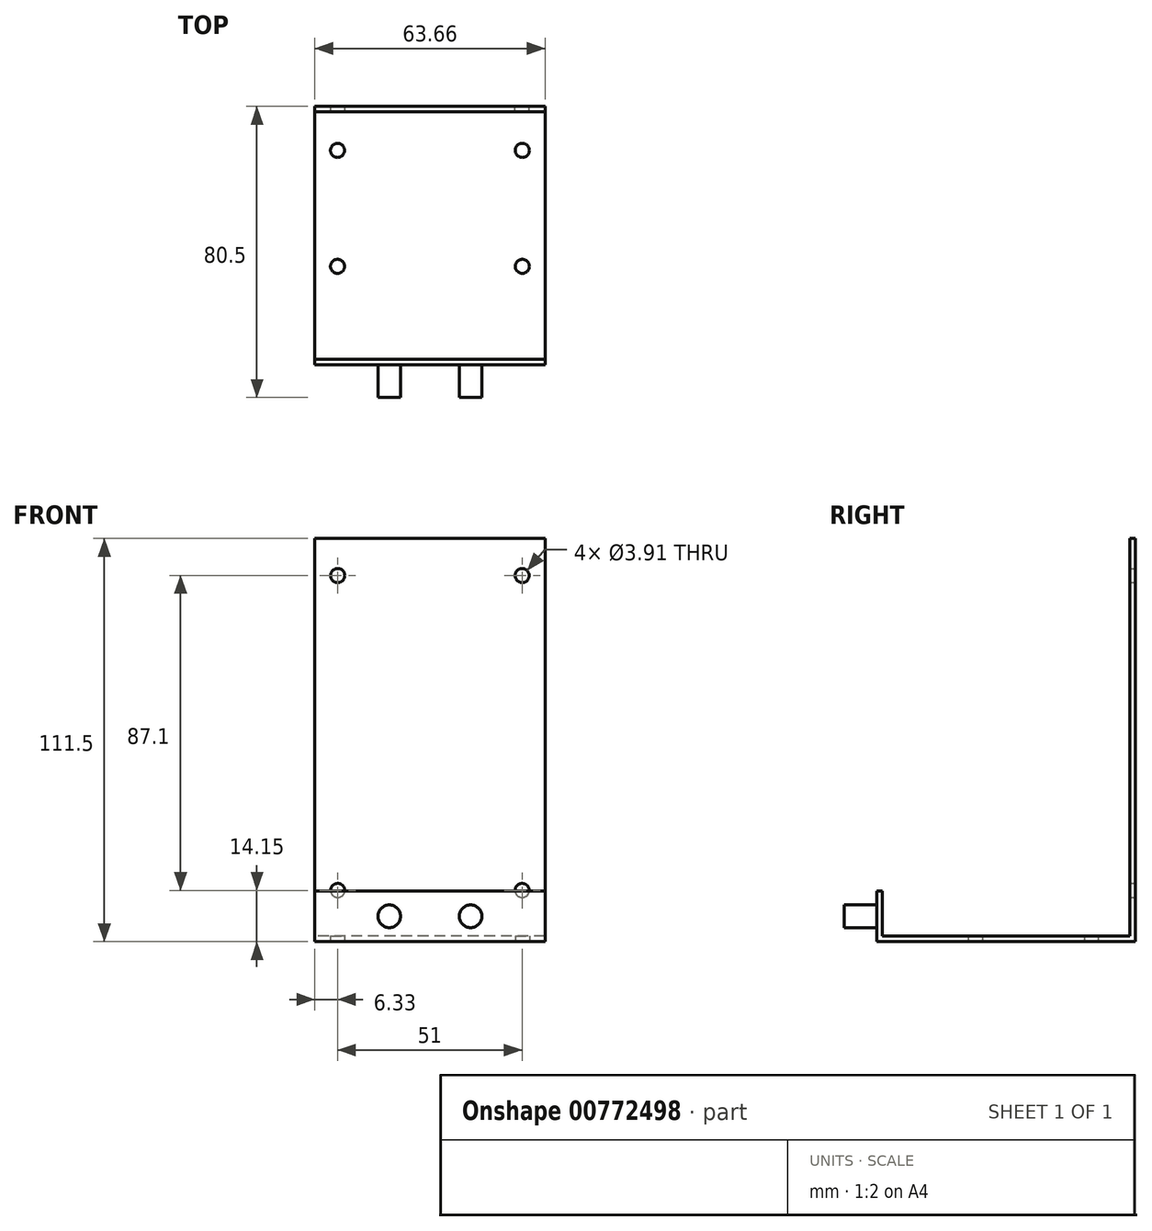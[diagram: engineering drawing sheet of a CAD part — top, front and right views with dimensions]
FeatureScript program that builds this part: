
annotation { "Feature Type Name" : "Feature", "Feature Type Description" : "" }
export const myFeature = defineFeature(function(context is Context, id is Id, definition is map)
    precondition{}
    {
        {
            var Q0;
            Q0=qCreatedBy(makeId("Right.planeOp"),FACE);
            var sketch = newSketch(context, id + "F0", { "sketchPlane" : qUnion([Q0])});
            skLineSegment(sketch, "E0", {"start": v(0, 111.5) * mm, "end": v(0, 0) * mm});
            skLineSegment(sketch, "E1", {"start": v(0, 0) * mm, "end": v(-71.5, 0) * mm});
            skLineSegment(sketch, "E2", {"start": v(-71.5, 0) * mm, "end": v(-71.5, 14) * mm});
            skLineSegment(sketch, "E3.0", {"start": v(-70, 1.5) * mm, "end": v(-70, 14) * mm});
            skLineSegment(sketch, "E3.1", {"start": v(-1.5, 1.5) * mm, "end": v(-70, 1.5) * mm});
            skLineSegment(sketch, "E3.2", {"start": v(-1.5, 111.5) * mm, "end": v(-1.5, 1.5) * mm});
            skLineSegment(sketch, "E4", {"start": v(-1.5, 111.5) * mm, "end": v(0, 111.5) * mm});
            skLineSegment(sketch, "E5", {"start": v(-70, 14) * mm, "end": v(-71.5, 14) * mm});
            skSolve(sketch);
        }
        {
            var Q0;
            Q0=makeQuery(id+"F0.imprint","IMPRINT",FACE,{"disambiguationData":[TD([[makeQuery(id+"F0.imprint","IMPRINT",EDGE,{"derivedFrom":sQuery(id+"F0.wireOp",EDGE,"E0")}),-1.0]])]});
            extrude(context, id + "F1", {"entities" : qUnion([Q0]), "depth" : (63.66 / 2) * mm, "offsetDistance" : 25 * mm, "hasSecondDirection" : true, "secondDirectionOppositeDirection" : true, "secondDirectionDepth" : (63.66 / 2) * mm});
        }
        {
            var Q0;
            Q0=makeQuery(id+"F1.opExtrude","SWEPT_FACE",FACE,{"disambiguationData":[OSD([sQuery(id+"F0.wireOp",EDGE,"E0")])]});
            var sketch = newSketch(context, id + "F2", { "sketchPlane" : qUnion([Q0])});
            skCircle(sketch, "E6", {"center": v(-25.5, 101.25) * mm, "radius": 1.96 * mm});
            skCircle(sketch, "E7", {"center": v(25.5, 101.25) * mm, "radius": 1.96 * mm});
            skCircle(sketch, "E8", {"center": v(25.5, 14.15) * mm, "radius": 1.96 * mm});
            skCircle(sketch, "E9", {"center": v(-25.5, 14.15) * mm, "radius": 1.96 * mm});
            skLineSegment(sketch, "E10", {"start": v(0, 111.5) * mm, "end": v(0, 89.93) * mm, "construction": true});
            skLineSegment(sketch, "E11", {"start": v(25.5, 101.25) * mm, "end": v(0, 101.25) * mm, "construction": true});
            skLineSegment(sketch, "E12", {"start": v(-25.5, 101.25) * mm, "end": v(0, 101.25) * mm, "construction": true});
            skSolve(sketch);
        }
        {
            var Q0;
            Q0 = qSketchRegion(id + "F2", true);
            extrude(context, id + "F3", {"entities" : qUnion([Q0]), "operationType" : NewBodyOperationType.REMOVE, "oppositeDirection" : true, "depth" : 25 * mm, "offsetDistance" : 25 * mm});
        }
        {
            var Q0;
            Q0=makeQuery(id+"F1.opExtrude","SWEPT_FACE",FACE,{"disambiguationData":[OSD([sQuery(id+"F0.wireOp",EDGE,"E2")])]});
            var sketch = newSketch(context, id + "F4", { "sketchPlane" : qUnion([Q0])});
            skLineSegment(sketch, "E13.0", {"start": v(-31.83, 0) * mm, "end": v(-31.83, 14) * mm, "construction": true});
            skLineSegment(sketch, "E14.0", {"start": v(31.83, 0) * mm, "end": v(31.83, 14) * mm, "construction": true});
            skCircle(sketch, "E15", {"center": v(-11.25, 7) * mm, "radius": 3.13 * mm});
            skCircle(sketch, "E16", {"center": v(11.25, 7) * mm, "radius": 3.13 * mm});
            skLineSegment(sketch, "E17", {"start": v(-11.25, 7) * mm, "end": v(-31.83, 7) * mm, "construction": true});
            skLineSegment(sketch, "E18", {"start": v(11.25, 7) * mm, "end": v(31.83, 7) * mm, "construction": true});
            skSolve(sketch);
        }
        {
            var Q0;
            Q0 = qSketchRegion(id + "F4", true);
            extrude(context, id + "F5", {"entities" : qUnion([Q0]), "operationType" : NewBodyOperationType.ADD, "depth" : 9 * mm, "offsetDistance" : 25 * mm});
        }
        {
            var Q0;
            Q0=makeQuery(id+"F1.opExtrude","SWEPT_FACE",FACE,{"disambiguationData":[OSD([sQuery(id+"F0.wireOp",EDGE,"E1")])]});
            var sketch = newSketch(context, id + "F6", { "sketchPlane" : qUnion([Q0])});
            skCircle(sketch, "E19", {"center": v(-25.55, 44.25) * mm, "radius": 1.95 * mm});
            skCircle(sketch, "E20", {"center": v(25.56, 44.25) * mm, "radius": 1.95 * mm});
            skCircle(sketch, "E21", {"center": v(25.55, 12.18) * mm, "radius": 1.95 * mm});
            skCircle(sketch, "E22", {"center": v(-25.56, 12.18) * mm, "radius": 1.95 * mm});
            skLineSegment(sketch, "E23", {"start": v(0, 0) * mm, "end": v(0, 60.73) * mm, "construction": true});
            skLineSegment(sketch, "E24", {"start": v(-25.56, 12.18) * mm, "end": v(0, 12.18) * mm, "construction": true});
            skLineSegment(sketch, "E25", {"start": v(25.55, 12.18) * mm, "end": v(0, 12.18) * mm, "construction": true});
            skSolve(sketch);
        }
        {
            var Q0;
            Q0 = qSketchRegion(id + "F6", true);
            extrude(context, id + "F7", {"entities" : qUnion([Q0]), "operationType" : NewBodyOperationType.REMOVE, "oppositeDirection" : true, "depth" : 25 * mm, "offsetDistance" : 25 * mm});
        }
    });
